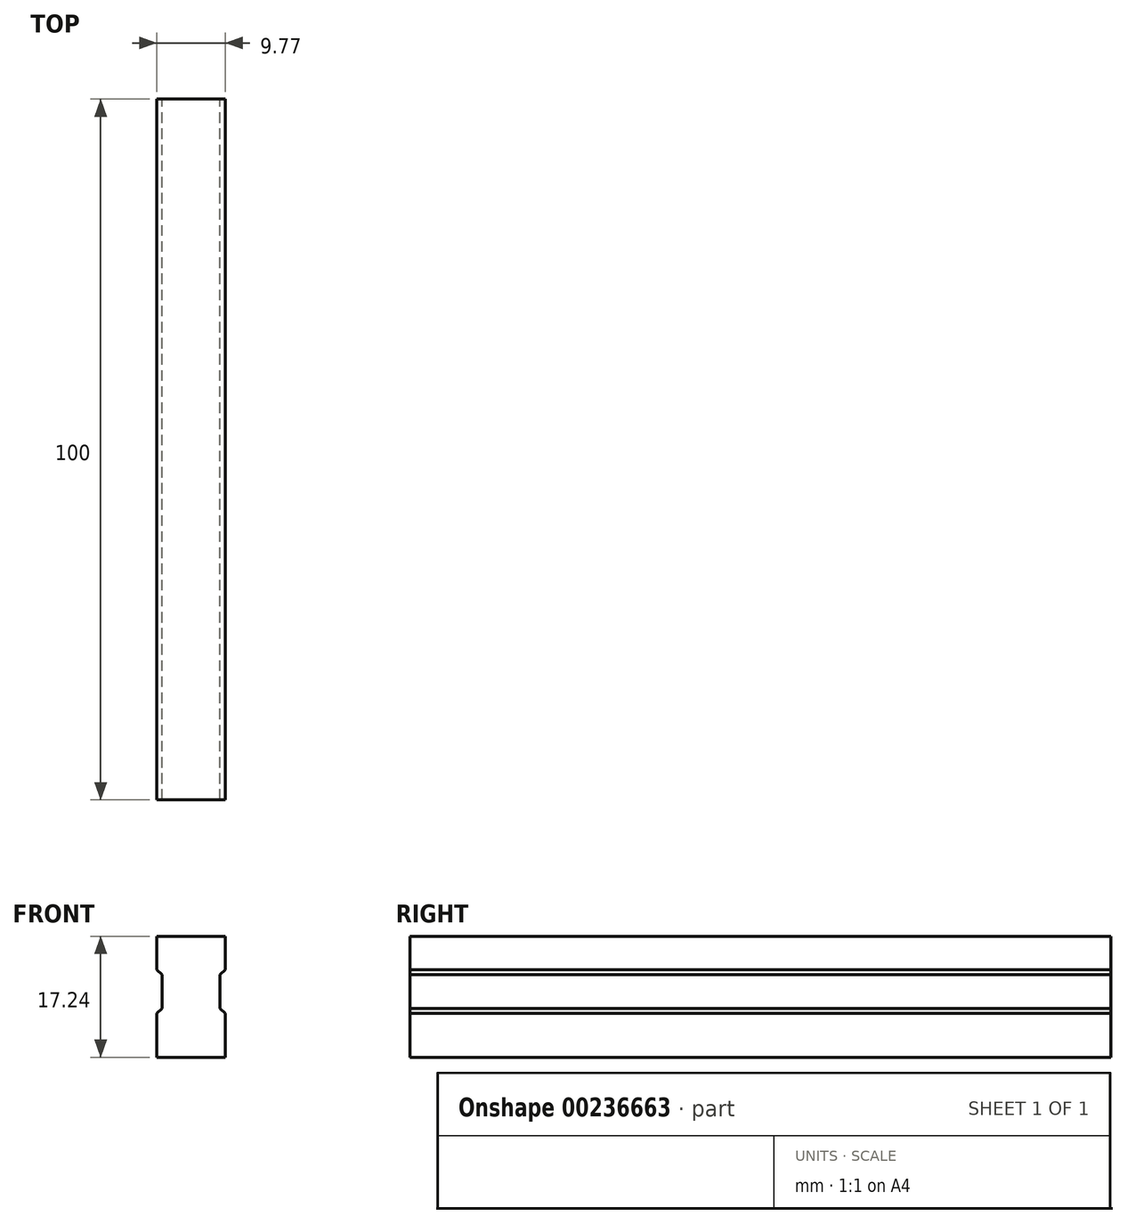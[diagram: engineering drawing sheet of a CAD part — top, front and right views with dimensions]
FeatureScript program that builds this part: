
annotation { "Feature Type Name" : "Feature", "Feature Type Description" : "" }
export const myFeature = defineFeature(function(context is Context, id is Id, definition is map)
    precondition{}
    {
        {
            var Q0;
            Q0=qCreatedBy(makeId("Front.planeOp"),FACE);
            var sketch = newSketch(context, id + "F0", { "sketchPlane" : qUnion([Q0])});
            skLineSegment(sketch, "E0.bottom", {"start": v(0, 0) * mm, "end": v(9.77, 0) * mm, "construction": true});
            skLineSegment(sketch, "E0.top", {"start": v(0, 17.24) * mm, "end": v(9.77, 17.24) * mm, "construction": true});
            skLineSegment(sketch, "E0.left", {"start": v(0, 0) * mm, "end": v(0, 17.24) * mm, "construction": true});
            skLineSegment(sketch, "E0.right", {"start": v(9.77, 0) * mm, "end": v(9.77, 17.24) * mm, "construction": true});
            skLineSegment(sketch, "E1", {"start": v(4.89, 17.24) * mm, "end": v(4.89, 0) * mm, "construction": true});
            skLineSegment(sketch, "E2", {"start": v(4.89, 0) * mm, "end": v(0, 0) * mm});
            skLineSegment(sketch, "E3", {"start": v(0, 6.26) * mm, "end": v(0.75, 6.95) * mm});
            skLineSegment(sketch, "E4", {"start": v(0.75, 6.95) * mm, "end": v(0.75, 11.78) * mm});
            skLineSegment(sketch, "E5", {"start": v(0.75, 11.78) * mm, "end": v(0, 12.47) * mm});
            skLineSegment(sketch, "E6", {"start": v(0, 12.47) * mm, "end": v(0, 17.24) * mm});
            skLineSegment(sketch, "E7", {"start": v(4.89, 17.24) * mm, "end": v(0, 17.24) * mm});
            skLineSegment(sketch, "E8", {"start": v(0, 0) * mm, "end": v(0, 6.26) * mm});
            skLineSegment(sketch, "E9.MirrorCS", {"start": v(9.02, 11.78) * mm, "end": v(9.77, 12.47) * mm});
            skLineSegment(sketch, "E10.MirrorCS", {"start": v(9.77, 6.26) * mm, "end": v(9.02, 6.95) * mm});
            skLineSegment(sketch, "E11.MirrorCS", {"start": v(9.77, 0) * mm, "end": v(9.77, 6.26) * mm});
            skLineSegment(sketch, "E12.MirrorCS", {"start": v(4.89, 17.24) * mm, "end": v(9.77, 17.24) * mm});
            skLineSegment(sketch, "E13.MirrorCS", {"start": v(4.89, 0) * mm, "end": v(9.77, 0) * mm});
            skLineSegment(sketch, "E14.MirrorCS", {"start": v(9.02, 6.95) * mm, "end": v(9.02, 11.78) * mm});
            skLineSegment(sketch, "E15.MirrorCS", {"start": v(9.77, 12.47) * mm, "end": v(9.77, 17.24) * mm});
            skSolve(sketch);
        }
        {
            var Q0;
            Q0=makeQuery(id+"F0.imprint","IMPRINT",FACE,{"disambiguationData":[TD([[makeQuery(id+"F0.imprint","IMPRINT",EDGE,{"derivedFrom":sQuery(id+"F0.wireOp",EDGE,"E2")}),-1.0]])]});
            extrude(context, id + "F1", {"entities" : qUnion([Q0]), "depth" : 100 * mm});
        }
    });
